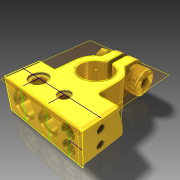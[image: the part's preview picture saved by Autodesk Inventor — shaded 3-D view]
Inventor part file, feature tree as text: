
AUTODESK INVENTOR PART (.ipt)
format: ipt  version: 2014 (Build 180170000, 170)  size: 800,256 bytes
history: native  units: in
note: dims shown in document units (in); Inventor stores cm internally (conversion verified against a paired STEP export)
features: sketch x14, projected_geometry x13, fillet x11, extrude x9, hole x7, other x6, chamfer x4, plane x3, surface_op x2, thread x2, mirror x1
ambient origin geometry x8: Origin, YZ Plane, XZ Plane, XY Plane, X Axis, Y Axis, Z Axis, Center Point
bodies: Solid1 (feature_tree)
feature tree (72):
  sketch  "Sketch1"  dims[d0=0.125in d2=0.375in]
  sketch  "Sketch2"  dims[d3=0.625in d4=0.5in d5=0.125in]
  plane  "Work Plane1"
  extrude  "Extrusion1"  Depth=0.125in
  surface_op  "Sculpt1"
  hole  "Hole1"  [1 undecoded]
  fillet  "Fillet1"  Radius=0.125in
  sketch  "Sketch4"  dims[d10=0.125in d11=1.0in d12=0.0in]
  hole  "Hole2"  [1 undecoded]
  hole  "Hole3"  [1 undecoded]
  hole  "Hole4"  [1 undecoded]
  extrude  "Extrusion3"  Depth=0.05in
  extrude  "Extrusion4"  Depth=0.03in
  mirror  "Mirror1"
  sketch  "Sketch8"  dims[d30=0.32in d31=0.75in d32=0.375in d33=0.25in d34=0.5635in d35=0.5in d36=0.0in]
  hole  "Hole5"  [1 undecoded]
  hole  "Hole6"  [1 undecoded]
  hole  "Hole7"  [1 undecoded]
  fillet  "Fillet3"  Radius=0.075in
  fillet  "Fillet4"  Radius=0.075in
  fillet  "Fillet5"  Radius=0.025in
  fillet  "Fillet6"  Radius=0.025in
  fillet  "Fillet7"  Radius=0.05in
  fillet  "Fillet8"  Radius=0.025in
  surface_op  "Sculpt2"
  extrude  "Extrusion5"  Depth=0.125in TaperAngle=0.0deg
  fillet  "Fillet9"  Radius=0.125in
  extrude  "Extrusion6"  [1 undecoded]
  chamfer  "Chamfer1"  Distance=0.28in
  plane  "Work Plane2"
  extrude  "Extrusion7"  Depth=0.125in TaperAngle=0.0deg
  thread  "Thread1"  [1 undecoded]
  thread  "Thread2"  [1 undecoded]
  chamfer  "Chamfer2"  Distance=0.1in
  extrude  "Extrusion8"  Depth=0.125in
  fillet  "Fillet10"  Radius=0.025in
  fillet  "Fillet11"  [1 undecoded]
  plane  "Work Plane3"
  extrude  "Extrusion9"  Depth=0.125in TaperAngle=0.0deg
  extrude  "Extrusion10"  Depth=0.125in
  fillet  "Fillet12"  Radius=0.075in
  chamfer  "Chamfer3"  Distance=0.125in
  chamfer  "Chamfer4"  Distance=0.01in
  sketch  "Sketch3"  dims[d8=0.0938in d9=0.1875in]
  projected_geometry  "Projected Loop1"
  projected_geometry  "Projected Loop2"
  sketch  "Sketch6"  dims[d13=0.25in d14=0.75in d15=0.375in d16=0.25in d17=0.5635in d18=1.0in d19=0.8108in d20=0.25in]
  sketch  "Sketch7"  dims[d23=0.425in d24=0.75in d25=0.375in d26=0.25in d27=0.5635in d28=0.5in d29=0.0in]
  projected_geometry  "Projected Loop4"
  projected_geometry  "Projected Loop5"
  projected_geometry  "Projected Loop6"
  projected_geometry  "Projected Loop7"
  sketch  "Sketch9"  dims[d37=0.1875in d38=0.75in d39=0.375in d40=0.25in d41=0.5635in d42=0.5in d43=0.0in d50=0.05in]
  projected_geometry  "Projected Loop8"
  projected_geometry  "Projected Loop9"
  projected_geometry  "Projected Loop10"
  sketch  "Sketch10"  dims[d51=0.05in d52=0.03in]
  sketch  "Sketch11"  dims[d53=0.03in d54=0.05in d55=0.0in]
  projected_geometry  "Projected Loop11"
  sketch  "Sketch12"  dims[d56=0.05in d57=0.0in]
  sketch  "Sketch13"  dims[d58=0.336in d59=0.75in d60=0.375in d61=0.25in d62=0.5635in d63=0.375in d64=0.0in]
  projected_geometry  "Projected Loop12"
  sketch  "Sketch14"  dims[d65=0.216in d66=0.75in d67=0.375in d68=0.25in d69=0.5635in d70=0.375in d71=0.0in]
  sketch  "Sketch15"  dims[d72=0.13in d73=0.75in d74=0.375in d75=0.25in d76=0.5635in d77=0.25in d78=0.0in d79=0.0625in d80=0.5in d81=0.075in d82=0.075in d83=0.025in d84=0.025in d85=0.05in d86=0.0in d87=0.025in d88=0.14in d89=0.0in d90=0.02in d91=0.125in d92=45.0deg d93=-0.04in d94=0.28in d95=0.0in d96=1.0in d97=0.0in d98=1.0in d99=0.0in d100=0.025in d101=0.125in d102=45.0deg d103=0.1in d104=0.0in d105=0.025in d106=0.025in d107=-0.0625in d108=0.225in d109=0.0in d110=0.075in d111=0.075in d112=0.125in d113=0.0in d114=0.01in d115=0.005in d116=0.125in d117=45.0deg d118=0.025in d119=0.125in d120=45.0deg]
  projected_geometry  "Projected Loop13"
  projected_geometry  "Projected Loop14"
  other  "Composite1"
  other  "Srf1"
  other  "Composite2"
  other  "Srf2"
  other  "Composite3"
  other  "Srf3"
note: 11 required parameter values undecoded (feature->parameter linkage not recoverable at this tier; creation-order binding heuristic only, values carry confidence <= 0.55)
